# Revit family: IS_Connect_E8231_BIM_DE
name_source: partatom
category: Plumbing Fixtures
revit_build: Autodesk Revit MEP 2016 (Build: 20161004_0715(x64)
units: mm (PartAtom-declared; Revit-internal decimal feet)

## family parameters
Always vertical = No
Cut with Voids When Loaded = No
OmniClass Number = 23.45.05.21.11.11
OmniClass Title = Water Operated Water Closets
Part Type = Normal
Room Calculation Point = No
Round Connector Dimension = Use Diameter
Shared = No
Work Plane-Based = No

## types (2) — shared parameters
Accessories = www.idealstandard.de\ersatzteile
AreaUnits = millimeters
AssetType = Fixed
BIMobject category = Toilets
BOSUseNativeGeometries = 1
Brand = Ideal Standard
Brand url = http://www.idealstandard.co.uk
CodePerformance = DIN EN 997 CL1-6A, DIN EN 33
ConnectionType = Plumbing
CurrencyUnit = €
CurrentRevision = 1
Date of publishing = 2017_11_20
DurationUnit = year
Edition number = 1
ExpectedLife = 25
Features = CONNECT floor standing bowl 360x545mm, wash-down
IFC Classification = Sanitary Terminal
IfcExportAs = IfcSanitaryTerminalType
IfcExportType = TOILETPANS
Installation instructions = http://www.idealstandard.de
InstallationInstructions = www.idealstandard.de\produkte
LinearUnits = millimeters
Manufacturer name = Ideal Standard
ManufacturerURL = www.idealstandard.com
Material = Vitreous china
Material main = Ceramics
NBS Reference Code = 35-93-94
NBS Reference Description = Wc Pans
Nominal height = 400
Nominal width = 360
NominalDepth = 545 mm  [stored 1.78806 ft]
NominalHeight = 400 mm  [stored 1.31234 ft]
NominalLength = 545 mm  [stored 1.78806 ft]
NominalWidth = 361 mm
OmniClass Code = 23-31 19 00
OmniClass Description = Toilets
PanMaterial = Vitreous china
Product Guid = be70e6f7-f41a-465a-8522-9ad86fab577e
Product SKU = E8231
Product certification = DIN EN 997 CL1-6A, DIN EN 33
Product data url = https://bimobject.com
Product family = CONNECT
Product group = Bowl
Product name = CONNECT floor standing bowl 360x545mm, wash-down
Product url = http://www.idealstandard.de
ProductInformation = www.idealstandard.de/produkte
QR code = http://bimobject.com
Shape = Sculptured
Size = 400 x 545 x 361mm
Space = Internal
SpareParts = www.idealstandard.de/ersatzteile
Technical description = http://www.idealstandard.de
ToiletType = WashDown
URL = http://www.idealstandard.de
Uniclass 1.4 Code = L7216
Uniclass 1.4 Description = Toilets
Uniclass 2.0 Code = PR-35-93-94
Uniclass 2.0 Description = Wc Pans
Uniclass 2015 Code = Pr_40_20_93_94
Uniclass 2015 Name = WC pans
Uniclass2015Code = Pr_40_20_93_94
Uniclass2015Title = WC pans
Uniclass2015Version = Products v1.1
Version = 1
VolumeUnits = Litres
Weight Net (Kg) = 25.35
zero-valued in all types: Cost, SpilloverLevel

## per-type parameters (varying)
| type | BIMObjectName | BarCode | Color | Description | EAN code | Finish | MainColor | Model | ModelNumber | ModelReference | Name | NettWeight | PanColor |
| E823101 - CONNECT floor standing bowl 360x545mm, wash-down | ISI_IdealStandard_WcPans_Connect_E823101 | 5017830448761 | White | E823101 CONNECT floor standing bowl 360x545mm, wash-down | 5017830448761 | White | White | E823101 | E823101 | E823101 CONNECT floor standing bowl 360x545mm, wash-down | WcPans_Connect_E823101_IdealStandard | 25,35 kg | White |
| E8231MA - CONNECT floor standing bowl 360x545mm, wash-down | ISI_IdealStandard_WcPans_Connect_E8231MA | 5017830448952 | WHITE IP | E8231MA CONNECT floor standing bowl 360x545mm, wash-down | 5017830448952 | WHITE IP | WHITE IP | E8231MA | E8231MA | E8231MA CONNECT floor standing bowl 360x545mm, wash-down | WcPans_Connect_E8231MA_IdealStandard | 23 kg | WHITE IP |

note: [stored X ft] marks values corroborated as IEEE doubles in the binary element streams (Revit-internal decimal feet)

## geometry (parser evidence)
native form markers: Blend x2, Sweep x3
no freeform markers — native parametric forms only
